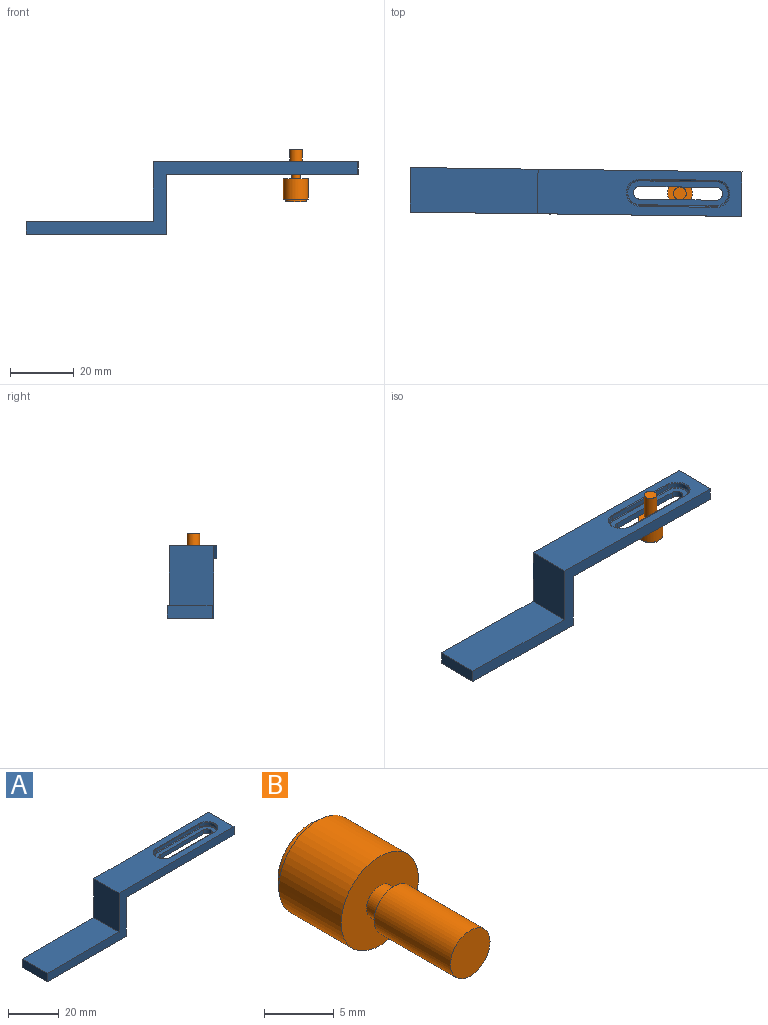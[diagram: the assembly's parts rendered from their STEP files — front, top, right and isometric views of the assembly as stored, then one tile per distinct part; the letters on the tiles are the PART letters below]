
ASSEMBLY  parts=2 mates=1
PART A: 27 faces, bbox 104x14x22.8 mm
  f0: plane 60.02x14mm, normal (0,0,-1), area 731.7mm2, adj f1,f2,f3,f4,f5,f6,f7,f23
  f1: plane 24x2mm, normal (0,1,0), area 48mm2, adj f0,f2,f4,f9
  f2: cylinder r=2mm len=4mm, axis (0,0,1), area 12.6mm2, adj f0,f1,f3,f9
  f3: plane 24x2mm, normal (0,-1,0), area 48mm2, adj f0,f2,f4,f9
  f4: cylinder r=2mm len=4mm, axis (0,0,1), area 12.6mm2, adj f0,f1,f3,f9
  f5: plane 14x4mm, normal (1,0,0), area 56mm2, adj f0,f6,f7,f8
  f6: plane 104.02x22.78mm, normal (0,1,0), area 491.2mm2, adj f0,f5,f8,f22,f23,f24,f25,f26
  f7: plane 104.02x22.78mm, normal (0,-1,0), area 491.2mm2, adj f0,f5,f8,f22,f23,f24,f25,f26
  f8: plane 64.02x14mm, normal (0,0,1), area 635.5mm2, adj f5,f6,f7,f14,f15,f16,f17,f22
  f9: plane 31.5x7.5mm, normal (0,0,1), area 115.6mm2, adj f1,f2,f3,f4,f18,f19,f20,f21
  f10: cylinder r=4mm len=8mm, axis (0,0,1), area 18.8mm2, adj f11,f13,f14,f18
  f11: plane 24x1.5mm, normal (0,-1,0), area 36mm2, adj f10,f12,f15,f19
  f12: cylinder r=4mm len=8mm, axis (0,0,1), area 18.8mm2, adj f11,f13,f17,f21
  f13: plane 24x1.5mm, normal (0,1,0), area 36mm2, adj f10,f12,f16,f20
  f14: torus R=4.25mm, axis (0,0,1), area 5mm2, adj f8,f10,f15,f16
  f15: cylinder r=0.25mm len=24mm, axis (1,0,0), area 9.4mm2, adj f8,f11,f14,f17
  f16: cylinder r=0.25mm len=24mm, axis (-1,0,0), area 9.4mm2, adj f8,f13,f14,f17
  f17: torus R=4.25mm, axis (0,0,1), area 5mm2, adj f8,f12,f15,f16
  f18: torus R=3.75mm, axis (0,0,1), area 4.8mm2, adj f9,f10,f19,f20
  f19: cylinder r=0.25mm len=24mm, axis (-1,0,0), area 9.4mm2, adj f9,f11,f18,f21
  f20: cylinder r=0.25mm len=24mm, axis (1,0,0), area 9.4mm2, adj f9,f13,f18,f21
  f21: torus R=3.75mm, axis (0,0,1), area 4.8mm2, adj f9,f12,f19,f20
  f22: plane 18.78x14mm, normal (-1,0,0), area 262.9mm2, adj f6,f7,f8,f25
  f23: plane 18.78x14mm, normal (1,0,0), area 262.9mm2, adj f0,f6,f7,f24
  f24: plane 44.01x14mm, normal (0,0,-1), area 616.1mm2, adj f6,f7,f23,f26
  f25: plane 40.01x14mm, normal (0,0,1), area 560.1mm2, adj f6,f7,f22,f26
  f26: plane 14x4mm, normal (-1,0,0), area 56mm2, adj f6,f7,f24,f25
PART B: 9 faces, bbox 7.8x16.2x7.8 mm
  f0: plane 4x4mm, normal (0,1,0), area 6.9mm2, adj f1,f8
  f1: cylinder r=1.34mm len=2.69mm, axis (0,-1,0), area 12.1mm2, adj f0,f2
  f2: plane 7.81x7.81mm, normal (0,-1,0), area 42.2mm2, adj f1,f3
  f3: cylinder r=3.91mm len=7.81mm, axis (0,-1,0), area 154.6mm2, adj f2,f4
  f4: plane 7.81x7.81mm, normal (0,1,0), area 15.7mm2, adj f3,f5
  f5: cylinder r=3.2mm len=6.4mm, axis (0,-1,0), area 15.9mm2, adj f4,f6
  f6: plane 6.4x6.4mm, normal (0,1,0), area 32.2mm2, adj f5
  f7: plane 4x4mm, normal (0,-1,0), area 12.6mm2, adj f8
  f8: cylinder r=2mm len=7.71mm, axis (0,-1,0), area 96.9mm2, adj f0,f7
PLACE A rot(axis=(0,0,-1),0.8deg) t=(-20.18,-19.46,0.87)mm
PLACE B rot(axis=(-0.67,0.52,-0.52),112.1deg) t=(3.43,-19.78,0.87)mm
MATE planar B.f1 <-> A.f0  axis (0,0,-1) through (3.43,-19.78,0.87)mm
